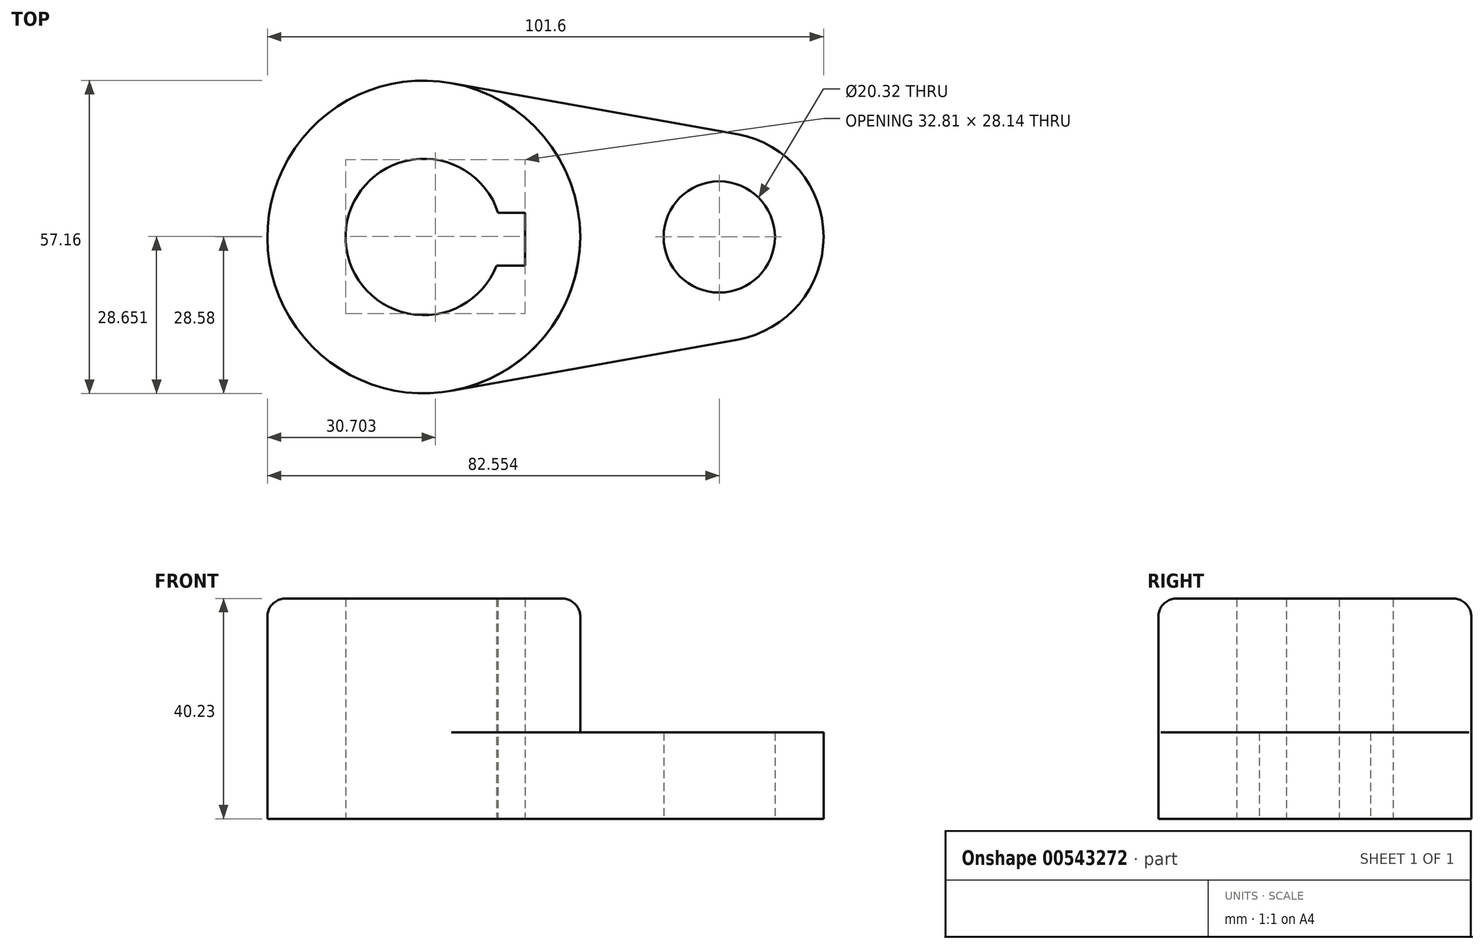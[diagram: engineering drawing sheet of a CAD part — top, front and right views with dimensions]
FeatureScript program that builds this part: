
annotation { "Feature Type Name" : "Feature", "Feature Type Description" : "" }
export const myFeature = defineFeature(function(context is Context, id is Id, definition is map)
    precondition{}
    {
        {
            var Q0;
            Q0=qCreatedBy(makeId("Top.planeOp"),FACE);
            var sketch = newSketch(context, id + "F0", { "sketchPlane" : qUnion([Q0])});
            skCircle(sketch, "E0", {"center": v(-31.32, 0) * mm, "radius": 14.29 * mm});
            skCircle(sketch, "E1", {"center": v(22.65, 0) * mm, "radius": 10.16 * mm});
            skCircle(sketch, "E2", {"center": v(-31.32, 0) * mm, "radius": 28.58 * mm});
            skCircle(sketch, "E3", {"center": v(22.65, 0) * mm, "radius": 19.05 * mm});
            skLineSegment(sketch, "E4", {"start": v(-26.28, 28.13) * mm, "end": v(26.02, 18.75) * mm});
            skLineSegment(sketch, "E5", {"start": v(-26.28, -28.13) * mm, "end": v(26.02, -18.75) * mm});
            skLineSegment(sketch, "E6.bottom", {"start": v(-31.32, 4.44) * mm, "end": v(-12.8, 4.44) * mm});
            skLineSegment(sketch, "E6.top", {"start": v(-31.32, -5.21) * mm, "end": v(-12.8, -5.21) * mm});
            skLineSegment(sketch, "E6.left", {"start": v(-31.32, 4.44) * mm, "end": v(-31.32, -5.21) * mm});
            skLineSegment(sketch, "E6.right", {"start": v(-12.8, 4.44) * mm, "end": v(-12.8, -5.21) * mm});
            skSolve(sketch);
        }
        {
            var Q0;
            {var subQ0=sQuery(id+"F0.wireOp",EDGE,"E4");Q0=makeQuery(id+"F0.imprint","IMPRINT",FACE,{"disambiguationData":[TD([[makeQuery(id+"F0.imprint","IMPRINT",EDGE,{"derivedFrom":subQ0}),-1.0]])]});}
            var Q1;
            {var subQ3=sQuery(id+"F0.wireOp",EDGE,"E6.right");Q1=makeQuery(id+"F0.imprint","IMPRINT",FACE,{"disambiguationData":[TD([[makeQuery(id+"F0.imprint","IMPRINT",EDGE,{"derivedFrom":subQ3}),1.0]])]});}
            var Q2;
            {var subQ5=sQuery(id+"F0.wireOp",EDGE,"E6.left");Q2=makeQuery(id+"F0.imprint","IMPRINT",FACE,{"disambiguationData":[TD([[makeQuery(id+"F0.imprint","IMPRINT",EDGE,{"derivedFrom":subQ5}),1.0]])]});}
            var Q3;
            Q3=makeQuery(id+"F0.imprint","IMPRINT",FACE,{"disambiguationData":[TD([[makeQuery(id+"F0.imprint","IMPRINT",EDGE,{"derivedFrom":sQuery(id+"F0.wireOp",EDGE,"E1")}),1.0]])]});
            var Q4;
            {var subQ5=sQuery(id+"F0.wireOp",EDGE,"E6.left");Q4=makeQuery(id+"F0.imprint","IMPRINT",FACE,{"disambiguationData":[TD([[makeQuery(id+"F0.imprint","IMPRINT",EDGE,{"derivedFrom":subQ5}),-1.0]])]});}
            var Q5;
            {var subQ5=sQuery(id+"F0.wireOp",EDGE,"E6.right");Q5=makeQuery(id+"F0.imprint","IMPRINT",FACE,{"disambiguationData":[TD([[makeQuery(id+"F0.imprint","IMPRINT",EDGE,{"derivedFrom":subQ5}),-1.0]])]});}
            var Q6;
            Q6=makeQuery(id+"F0.imprint","IMPRINT",FACE,{"disambiguationData":[TD([[makeQuery(id+"F0.imprint","IMPRINT",EDGE,{"derivedFrom":sQuery(id+"F0.wireOp",EDGE,"E1")}),-1.0]])]});
            extrude(context, id + "F1", {"entities" : qUnion([Q0, Q1, Q2, Q3, Q4, Q5, Q6]), "depth" : 15.77 * mm, "offsetDistance" : 25.4 * mm});
        }
        {
            var Q0;
            {var subQ3=sQuery(id+"F0.wireOp",EDGE,"E6.right");Q0=makeQuery(id+"F0.imprint","IMPRINT",FACE,{"disambiguationData":[TD([[makeQuery(id+"F0.imprint","IMPRINT",EDGE,{"derivedFrom":subQ3}),1.0]])]});}
            extrude(context, id + "F2", {"entities" : qUnion([Q0]), "operationType" : NewBodyOperationType.ADD, "depth" : 40.23 * mm, "offsetDistance" : 25.4 * mm});
        }
        {
            var Q0;
            {var subQ5=sQuery(id+"F0.wireOp",EDGE,"E6.left");Q0=makeQuery(id+"F0.imprint","IMPRINT",FACE,{"disambiguationData":[TD([[makeQuery(id+"F0.imprint","IMPRINT",EDGE,{"derivedFrom":subQ5}),1.0]])]});}
            var Q1;
            {var subQ5=sQuery(id+"F0.wireOp",EDGE,"E6.right");Q1=makeQuery(id+"F0.imprint","IMPRINT",FACE,{"disambiguationData":[TD([[makeQuery(id+"F0.imprint","IMPRINT",EDGE,{"derivedFrom":subQ5}),-1.0]])]});}
            var Q2;
            {var subQ5=sQuery(id+"F0.wireOp",EDGE,"E6.left");Q2=makeQuery(id+"F0.imprint","IMPRINT",FACE,{"disambiguationData":[TD([[makeQuery(id+"F0.imprint","IMPRINT",EDGE,{"derivedFrom":subQ5}),-1.0]])]});}
            extrude(context, id + "F3", {"entities" : qUnion([Q0, Q1, Q2]), "operationType" : NewBodyOperationType.REMOVE, "endBound" : BoundingType.THROUGH_ALL, "depth" : 25.4 * mm, "offsetDistance" : 25.4 * mm});
        }
        {
            var Q0;
            Q0=makeQuery(id+"F0.imprint","IMPRINT",FACE,{"disambiguationData":[TD([[makeQuery(id+"F0.imprint","IMPRINT",EDGE,{"derivedFrom":sQuery(id+"F0.wireOp",EDGE,"E1")}),1.0]])]});
            extrude(context, id + "F4", {"entities" : qUnion([Q0]), "operationType" : NewBodyOperationType.REMOVE, "depth" : 25.4 * mm, "offsetDistance" : 25.4 * mm});
        }
        {
            var Q0;
            Q0=makeQuery(id+"F2.opExtrude","CAP_EDGE",EDGE,{"disambiguationData":[OSD([sQuery(id+"F0.wireOp",EDGE,"E2")])],"isStart":false});
            fillet(context, id + "F5", {"entities" : qUnion([Q0]), "radius" : 3.3 * mm, "tangentPropagation" : true, "allowEdgeOverflow" : false});
        }
    });
